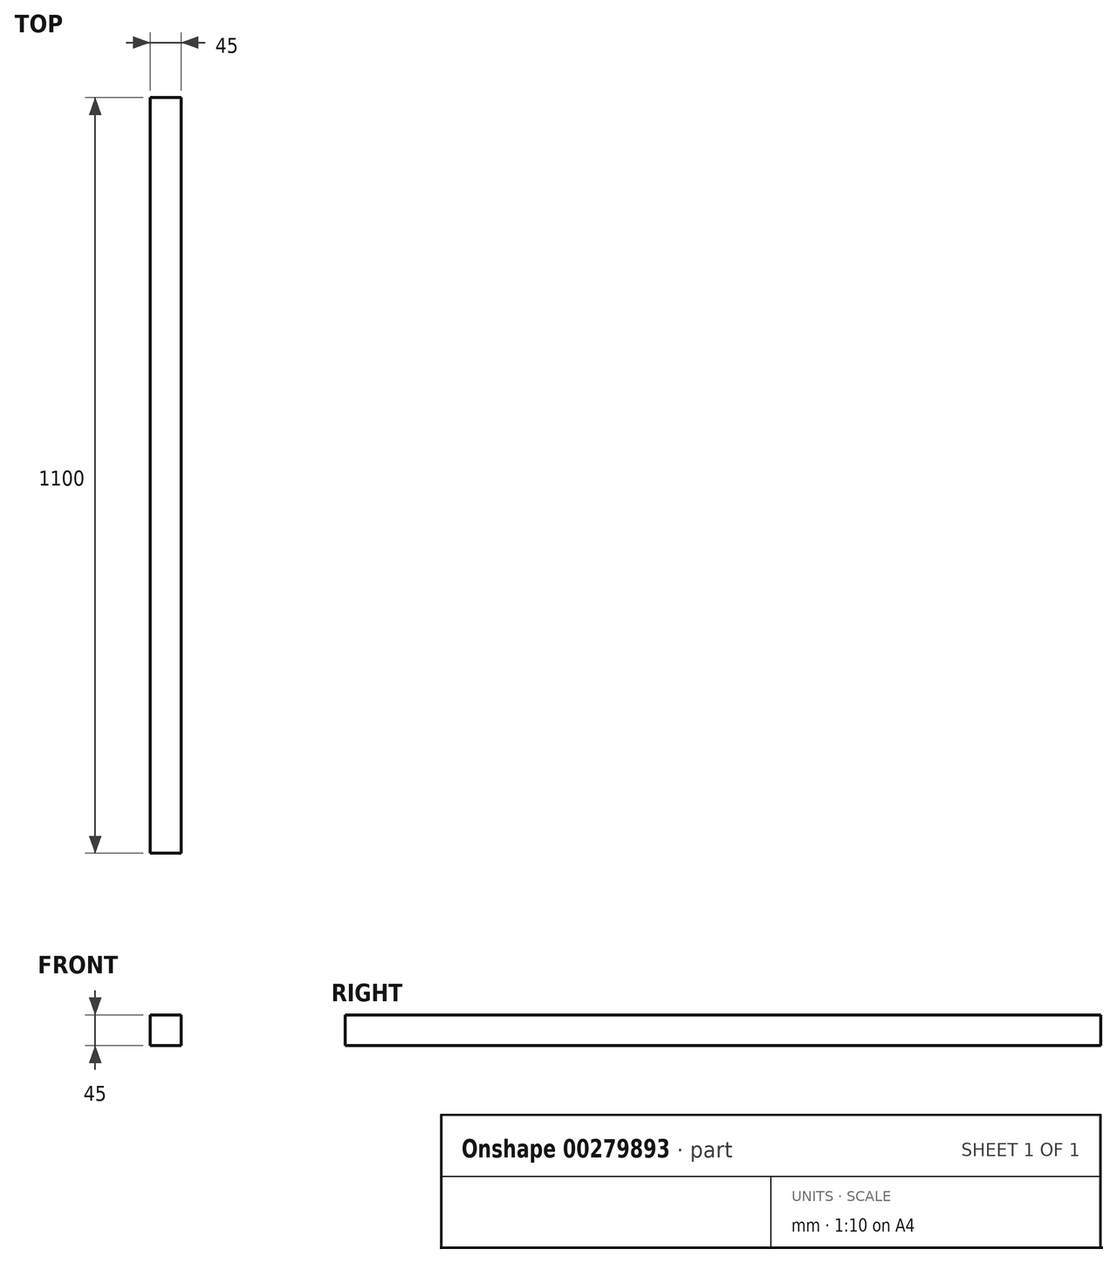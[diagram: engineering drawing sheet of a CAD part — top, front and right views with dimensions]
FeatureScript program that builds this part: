
annotation { "Feature Type Name" : "Feature", "Feature Type Description" : "" }
export const myFeature = defineFeature(function(context is Context, id is Id, definition is map)
    precondition{}
    {
        {
            var Q0;
            Q0=qCreatedBy(makeId("Front.planeOp"),FACE);
            var sketch = newSketch(context, id + "F0", { "sketchPlane" : qUnion([Q0])});
            skLineSegment(sketch, "E0.bottom", {"start": v(-22.5, 22.5) * mm, "end": v(22.5, 22.5) * mm});
            skLineSegment(sketch, "E0.top", {"start": v(-22.5, -22.5) * mm, "end": v(22.5, -22.5) * mm});
            skLineSegment(sketch, "E0.left", {"start": v(-22.5, 22.5) * mm, "end": v(-22.5, -22.5) * mm});
            skLineSegment(sketch, "E0.right", {"start": v(22.5, 22.5) * mm, "end": v(22.5, -22.5) * mm});
            skSolve(sketch);
        }
        {
            var Q0;
            Q0=makeQuery(id+"F0.imprint","IMPRINT",FACE,{"disambiguationData":[TD([[makeQuery(id+"F0.imprint","IMPRINT",EDGE,{"derivedFrom":sQuery(id+"F0.wireOp",EDGE,"E0.bottom")}),-1.0]])]});
            extrude(context, id + "F1", {"entities" : qUnion([Q0]), "depth" : 1100 * mm});
        }
    });
